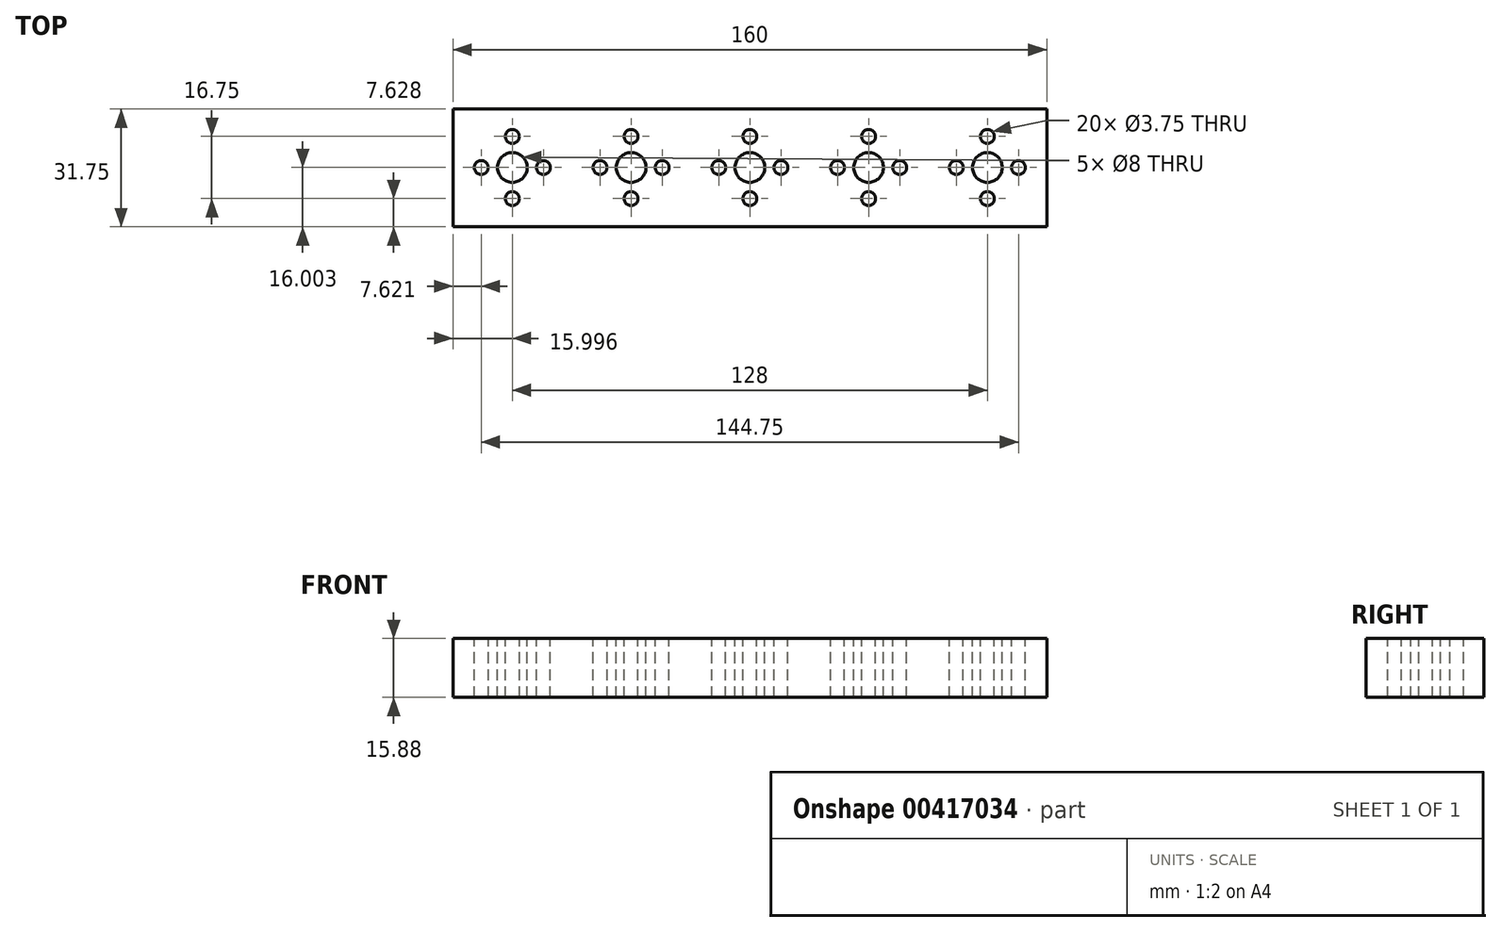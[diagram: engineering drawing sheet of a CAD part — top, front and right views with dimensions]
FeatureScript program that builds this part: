
annotation { "Feature Type Name" : "Feature", "Feature Type Description" : "" }
export const myFeature = defineFeature(function(context is Context, id is Id, definition is map)
    precondition{}
    {
        {
            var Q0;
            Q0=qCreatedBy(makeId("Top.planeOp"),FACE);
            var sketch = newSketch(context, id + "F0", { "sketchPlane" : qUnion([Q0])});
            skLineSegment(sketch, "E0.bottom", {"start": v(-86.72, 5.6) * mm, "end": v(73.28, 5.6) * mm});
            skLineSegment(sketch, "E0.top", {"start": v(-86.72, -26.16) * mm, "end": v(73.28, -26.16) * mm});
            skLineSegment(sketch, "E0.left", {"start": v(-86.72, 5.6) * mm, "end": v(-86.72, -26.16) * mm});
            skLineSegment(sketch, "E0.right", {"start": v(73.28, 5.6) * mm, "end": v(73.28, -26.16) * mm});
            skSolve(sketch);
        }
        {
            var Q0;
            Q0=makeQuery(id+"F0.imprint","IMPRINT",FACE,{"disambiguationData":[TD([[makeQuery(id+"F0.imprint","IMPRINT",EDGE,{"derivedFrom":sQuery(id+"F0.wireOp",EDGE,"E0.bottom")}),-1.0]])]});
            extrude(context, id + "F1", {"entities" : qUnion([Q0]), "depth" : 15.88 * mm});
        }
        {
            var Q0;
            Q0=makeQuery(id+"F1.opExtrude","CAP_FACE",FACE,{"disambiguationData":[OSD([sQuery(id+"F0.wireOp",EDGE,"E0.bottom"),sQuery(id+"F0.wireOp",EDGE,"E0.top"),sQuery(id+"F0.wireOp",EDGE,"E0.left"),sQuery(id+"F0.wireOp",EDGE,"E0.right")])],"isStart":false});
            var sketch = newSketch(context, id + "F2", { "sketchPlane" : qUnion([Q0])});
            skCircle(sketch, "E1", {"center": v(57.28, -10.16) * mm, "radius": 4 * mm});
            skCircle(sketch, "E2", {"center": v(57.28, -18.53) * mm, "radius": 1.88 * mm});
            skLineSegment(sketch, "E3.0.0", {"start": v(-86.72, 5.6) * mm, "end": v(-86.72, -26.16) * mm});
            skLineSegment(sketch, "E3.0.1", {"start": v(-86.72, -26.16) * mm, "end": v(73.28, -26.16) * mm});
            skLineSegment(sketch, "E3.0.2", {"start": v(73.28, -26.16) * mm, "end": v(73.28, 5.6) * mm});
            skLineSegment(sketch, "E3.0.3", {"start": v(73.28, 5.6) * mm, "end": v(-86.72, 5.6) * mm});
            skCircle(sketch, "E4.1.0", {"center": v(65.65, -10.16) * mm, "radius": 1.88 * mm});
            skCircle(sketch, "E4.2.0", {"center": v(57.28, -1.78) * mm, "radius": 1.88 * mm});
            skCircle(sketch, "E4.3.0", {"center": v(48.9, -10.16) * mm, "radius": 1.88 * mm});
            skCircle(sketch, "E5.1.0.0", {"center": v(25.28, -10.16) * mm, "radius": 4 * mm});
            skCircle(sketch, "E5.1.0.1", {"center": v(16.9, -10.16) * mm, "radius": 1.88 * mm});
            skCircle(sketch, "E5.1.0.2", {"center": v(25.28, -1.78) * mm, "radius": 1.88 * mm});
            skCircle(sketch, "E5.1.0.3", {"center": v(33.65, -10.16) * mm, "radius": 1.88 * mm});
            skCircle(sketch, "E5.1.0.4", {"center": v(25.28, -18.53) * mm, "radius": 1.88 * mm});
            skCircle(sketch, "E5.2.0.0", {"center": v(-6.72, -10.16) * mm, "radius": 4 * mm});
            skCircle(sketch, "E5.2.0.1", {"center": v(-15.1, -10.16) * mm, "radius": 1.88 * mm});
            skCircle(sketch, "E5.2.0.2", {"center": v(-6.72, -1.78) * mm, "radius": 1.88 * mm});
            skCircle(sketch, "E5.2.0.3", {"center": v(1.65, -10.16) * mm, "radius": 1.88 * mm});
            skCircle(sketch, "E5.2.0.4", {"center": v(-6.72, -18.53) * mm, "radius": 1.88 * mm});
            skCircle(sketch, "E5.3.0.0", {"center": v(-38.72, -10.16) * mm, "radius": 4 * mm});
            skCircle(sketch, "E5.3.0.1", {"center": v(-47.1, -10.16) * mm, "radius": 1.88 * mm});
            skCircle(sketch, "E5.3.0.2", {"center": v(-38.72, -1.78) * mm, "radius": 1.88 * mm});
            skCircle(sketch, "E5.3.0.3", {"center": v(-30.35, -10.16) * mm, "radius": 1.88 * mm});
            skCircle(sketch, "E5.3.0.4", {"center": v(-38.72, -18.53) * mm, "radius": 1.88 * mm});
            skCircle(sketch, "E5.4.0.0", {"center": v(-70.72, -10.16) * mm, "radius": 4 * mm});
            skCircle(sketch, "E5.4.0.1", {"center": v(-79.1, -10.16) * mm, "radius": 1.88 * mm});
            skCircle(sketch, "E5.4.0.2", {"center": v(-70.72, -1.78) * mm, "radius": 1.88 * mm});
            skCircle(sketch, "E5.4.0.3", {"center": v(-62.35, -10.16) * mm, "radius": 1.88 * mm});
            skCircle(sketch, "E5.4.0.4", {"center": v(-70.72, -18.53) * mm, "radius": 1.88 * mm});
            skLineSegment(sketch, "E5.direction1", {"start": v(57.28, -10.16) * mm, "end": v(25.28, -10.16) * mm, "construction": true});
            skSolve(sketch);
        }
        {
            var Q0;
            Q0=makeQuery(id+"F2.imprint","IMPRINT",FACE,{"disambiguationData":[TD([[makeQuery(id+"F2.imprint","IMPRINT",EDGE,{"derivedFrom":sQuery(id+"F2.wireOp",EDGE,"E5.4.0.0")}),1.0]])]});
            var Q1;
            Q1=makeQuery(id+"F2.imprint","IMPRINT",FACE,{"disambiguationData":[TD([[makeQuery(id+"F2.imprint","IMPRINT",EDGE,{"derivedFrom":sQuery(id+"F2.wireOp",EDGE,"E5.4.0.2")}),1.0]])]});
            var Q2;
            Q2=makeQuery(id+"F2.imprint","IMPRINT",FACE,{"disambiguationData":[TD([[makeQuery(id+"F2.imprint","IMPRINT",EDGE,{"derivedFrom":sQuery(id+"F2.wireOp",EDGE,"E5.4.0.1")}),1.0]])]});
            var Q3;
            Q3=makeQuery(id+"F2.imprint","IMPRINT",FACE,{"disambiguationData":[TD([[makeQuery(id+"F2.imprint","IMPRINT",EDGE,{"derivedFrom":sQuery(id+"F2.wireOp",EDGE,"E5.4.0.4")}),1.0]])]});
            var Q4;
            Q4=makeQuery(id+"F2.imprint","IMPRINT",FACE,{"disambiguationData":[TD([[makeQuery(id+"F2.imprint","IMPRINT",EDGE,{"derivedFrom":sQuery(id+"F2.wireOp",EDGE,"E5.4.0.3")}),1.0]])]});
            var Q5;
            Q5=makeQuery(id+"F2.imprint","IMPRINT",FACE,{"disambiguationData":[TD([[makeQuery(id+"F2.imprint","IMPRINT",EDGE,{"derivedFrom":sQuery(id+"F2.wireOp",EDGE,"E5.3.0.0")}),1.0]])]});
            var Q6;
            Q6=makeQuery(id+"F2.imprint","IMPRINT",FACE,{"disambiguationData":[TD([[makeQuery(id+"F2.imprint","IMPRINT",EDGE,{"derivedFrom":sQuery(id+"F2.wireOp",EDGE,"E5.3.0.2")}),1.0]])]});
            var Q7;
            Q7=makeQuery(id+"F2.imprint","IMPRINT",FACE,{"disambiguationData":[TD([[makeQuery(id+"F2.imprint","IMPRINT",EDGE,{"derivedFrom":sQuery(id+"F2.wireOp",EDGE,"E5.3.0.1")}),1.0]])]});
            var Q8;
            Q8=makeQuery(id+"F2.imprint","IMPRINT",FACE,{"disambiguationData":[TD([[makeQuery(id+"F2.imprint","IMPRINT",EDGE,{"derivedFrom":sQuery(id+"F2.wireOp",EDGE,"E5.3.0.4")}),1.0]])]});
            var Q9;
            Q9=makeQuery(id+"F2.imprint","IMPRINT",FACE,{"disambiguationData":[TD([[makeQuery(id+"F2.imprint","IMPRINT",EDGE,{"derivedFrom":sQuery(id+"F2.wireOp",EDGE,"E5.3.0.3")}),1.0]])]});
            var Q10;
            Q10=makeQuery(id+"F2.imprint","IMPRINT",FACE,{"disambiguationData":[TD([[makeQuery(id+"F2.imprint","IMPRINT",EDGE,{"derivedFrom":sQuery(id+"F2.wireOp",EDGE,"E5.2.0.0")}),1.0]])]});
            var Q11;
            Q11=makeQuery(id+"F2.imprint","IMPRINT",FACE,{"disambiguationData":[TD([[makeQuery(id+"F2.imprint","IMPRINT",EDGE,{"derivedFrom":sQuery(id+"F2.wireOp",EDGE,"E5.2.0.1")}),1.0]])]});
            var Q12;
            Q12=makeQuery(id+"F2.imprint","IMPRINT",FACE,{"disambiguationData":[TD([[makeQuery(id+"F2.imprint","IMPRINT",EDGE,{"derivedFrom":sQuery(id+"F2.wireOp",EDGE,"E5.2.0.2")}),1.0]])]});
            var Q13;
            Q13=makeQuery(id+"F2.imprint","IMPRINT",FACE,{"disambiguationData":[TD([[makeQuery(id+"F2.imprint","IMPRINT",EDGE,{"derivedFrom":sQuery(id+"F2.wireOp",EDGE,"E5.2.0.4")}),1.0]])]});
            var Q14;
            Q14=makeQuery(id+"F2.imprint","IMPRINT",FACE,{"disambiguationData":[TD([[makeQuery(id+"F2.imprint","IMPRINT",EDGE,{"derivedFrom":sQuery(id+"F2.wireOp",EDGE,"E5.2.0.3")}),1.0]])]});
            var Q15;
            Q15=makeQuery(id+"F2.imprint","IMPRINT",FACE,{"disambiguationData":[TD([[makeQuery(id+"F2.imprint","IMPRINT",EDGE,{"derivedFrom":sQuery(id+"F2.wireOp",EDGE,"E5.1.0.0")}),1.0]])]});
            var Q16;
            Q16=makeQuery(id+"F2.imprint","IMPRINT",FACE,{"disambiguationData":[TD([[makeQuery(id+"F2.imprint","IMPRINT",EDGE,{"derivedFrom":sQuery(id+"F2.wireOp",EDGE,"E5.1.0.1")}),1.0]])]});
            var Q17;
            Q17=makeQuery(id+"F2.imprint","IMPRINT",FACE,{"disambiguationData":[TD([[makeQuery(id+"F2.imprint","IMPRINT",EDGE,{"derivedFrom":sQuery(id+"F2.wireOp",EDGE,"E5.1.0.2")}),1.0]])]});
            var Q18;
            Q18=makeQuery(id+"F2.imprint","IMPRINT",FACE,{"disambiguationData":[TD([[makeQuery(id+"F2.imprint","IMPRINT",EDGE,{"derivedFrom":sQuery(id+"F2.wireOp",EDGE,"E5.1.0.4")}),1.0]])]});
            var Q19;
            Q19=makeQuery(id+"F2.imprint","IMPRINT",FACE,{"disambiguationData":[TD([[makeQuery(id+"F2.imprint","IMPRINT",EDGE,{"derivedFrom":sQuery(id+"F2.wireOp",EDGE,"E1")}),1.0]])]});
            var Q20;
            Q20=makeQuery(id+"F2.imprint","IMPRINT",FACE,{"disambiguationData":[TD([[makeQuery(id+"F2.imprint","IMPRINT",EDGE,{"derivedFrom":sQuery(id+"F2.wireOp",EDGE,"E4.3.0")}),1.0]])]});
            var Q21;
            Q21=makeQuery(id+"F2.imprint","IMPRINT",FACE,{"disambiguationData":[TD([[makeQuery(id+"F2.imprint","IMPRINT",EDGE,{"derivedFrom":sQuery(id+"F2.wireOp",EDGE,"E2")}),1.0]])]});
            var Q22;
            Q22=makeQuery(id+"F2.imprint","IMPRINT",FACE,{"disambiguationData":[TD([[makeQuery(id+"F2.imprint","IMPRINT",EDGE,{"derivedFrom":sQuery(id+"F2.wireOp",EDGE,"E4.1.0")}),1.0]])]});
            var Q23;
            Q23=makeQuery(id+"F2.imprint","IMPRINT",FACE,{"disambiguationData":[TD([[makeQuery(id+"F2.imprint","IMPRINT",EDGE,{"derivedFrom":sQuery(id+"F2.wireOp",EDGE,"E4.2.0")}),1.0]])]});
            var Q24;
            Q24=makeQuery(id+"F2.imprint","IMPRINT",FACE,{"disambiguationData":[TD([[makeQuery(id+"F2.imprint","IMPRINT",EDGE,{"derivedFrom":sQuery(id+"F2.wireOp",EDGE,"E5.1.0.3")}),1.0]])]});
            extrude(context, id + "F3", {"entities" : qUnion([Q0, Q1, Q2, Q3, Q4, Q5, Q6, Q7, Q8, Q9, Q10, Q11, Q12, Q13, Q14, Q15, Q16, Q17, Q18, Q19, Q20, Q21, Q22, Q23, Q24]), "operationType" : NewBodyOperationType.REMOVE, "oppositeDirection" : true, "depth" : 25.4 * mm});
        }
    });
